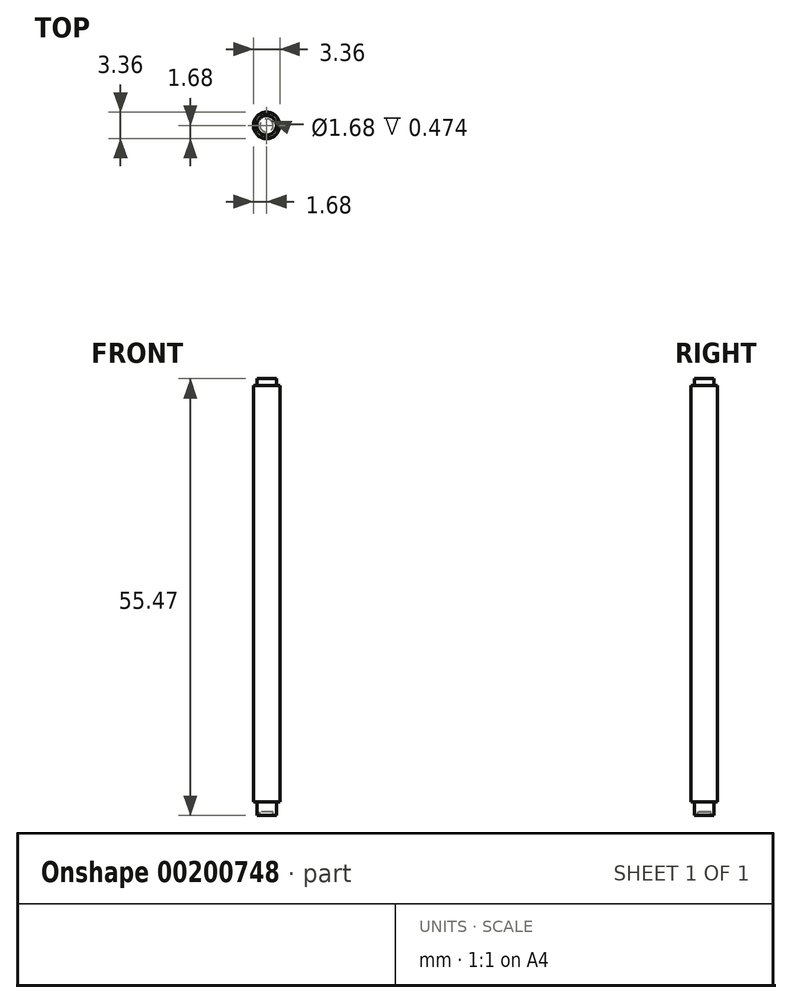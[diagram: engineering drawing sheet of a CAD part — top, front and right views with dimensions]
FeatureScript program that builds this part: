
annotation { "Feature Type Name" : "Feature", "Feature Type Description" : "" }
export const myFeature = defineFeature(function(context is Context, id is Id, definition is map)
    precondition{}
    {
        {
            var Q0;
            Q0=qCreatedBy(makeId("Front.planeOp"),FACE);
            var sketch = newSketch(context, id + "F0", { "sketchPlane" : qUnion([Q0])});
            skLineSegment(sketch, "E0", {"start": v(0, 1.34) * mm, "end": v(0, -7.33) * mm});
            skLineSegment(sketch, "E1", {"start": v(0.84, -7.33) * mm, "end": v(0.84, -9.37) * mm});
            skLineSegment(sketch, "E2", {"start": v(0, -7.33) * mm, "end": v(0, -10.92) * mm});
            skLineSegment(sketch, "E3", {"start": v(0, -10.92) * mm, "end": v(0, -7.33) * mm});
            skArc(sketch, "E4", {"start": v(0.84, -9.37) * mm, "mid": v(0.62, -10.26) * mm, "end": v(0, -10.92) * mm});
            skLineSegment(sketch, "E5", {"start": v(1.23, -7.33) * mm, "end": v(1.23, -7.8) * mm});
            skLineSegment(sketch, "E6", {"start": v(1.23, -7.8) * mm, "end": v(0.84, -7.8) * mm});
            skLineSegment(sketch, "E7", {"start": v(0, 46.79) * mm, "end": v(1.68, 46.79) * mm});
            skLineSegment(sketch, "E8", {"start": v(0, 46.79) * mm, "end": v(0, 1.34) * mm});
            skLineSegment(sketch, "E9", {"start": v(0, 46.79) * mm, "end": v(0, 47.67) * mm});
            skLineSegment(sketch, "E10", {"start": v(0, 47.67) * mm, "end": v(1.24, 47.67) * mm});
            skLineSegment(sketch, "E11", {"start": v(1.24, 47.67) * mm, "end": v(1.24, 46.79) * mm});
            skLineSegment(sketch, "E12", {"start": v(1.23, -7.33) * mm, "end": v(1.23, -6.06) * mm});
            skLineSegment(sketch, "E13", {"start": v(1.23, -6.06) * mm, "end": v(1.68, -6.06) * mm});
            skLineSegment(sketch, "E14", {"start": v(1.68, -6.06) * mm, "end": v(1.68, 46.79) * mm});
            skLineSegment(sketch, "E15", {"start": v(0, -7.33) * mm, "end": v(1.23, -7.33) * mm});
            skSolve(sketch);
        }
        {
            var Q0;
            {var subQ4=sQuery(id+"F0.wireOp",EDGE,"E0");Q0=makeQuery(id+"F0.imprint","IMPRINT",FACE,{"disambiguationData":[TD([[makeQuery(id+"F0.imprint","IMPRINT",EDGE,{"derivedFrom":subQ4}),1.0]])]});}
            var Q1;
            {var subQ1=sQuery(id+"F0.wireOp",EDGE,"E3");Q1=makeQuery(id+"F0.imprint","IMPRINT",FACE,{"disambiguationData":[TD([[makeQuery(id+"F0.imprint","IMPRINT",EDGE,{"derivedFrom":subQ1}),-1.0]])]});}
            var Q2;
            {var subQ0=sQuery(id+"F0.wireOp",EDGE,"E9");Q2=makeQuery(id+"F0.imprint","IMPRINT",FACE,{"disambiguationData":[TD([[makeQuery(id+"F0.imprint","IMPRINT",EDGE,{"derivedFrom":subQ0}),-1.0]])]});}
            var Q3;
            {var subQ4=sQuery(id+"F0.wireOp",EDGE,"E5");Q3=makeQuery(id+"F0.imprint","IMPRINT",FACE,{"disambiguationData":[TD([[makeQuery(id+"F0.imprint","IMPRINT",EDGE,{"derivedFrom":subQ4}),-1.0]])]});}
            var Q4;
            Q4=sQuery(id+"F0.wireOp",EDGE,"E8");
            revolve(context, id + "F1", {"entities" : qUnion([Q0, Q1, Q2, Q3]), "axis" : qUnion([Q4]), "revolveType" : RevolveType.FULL});
        }
    });
